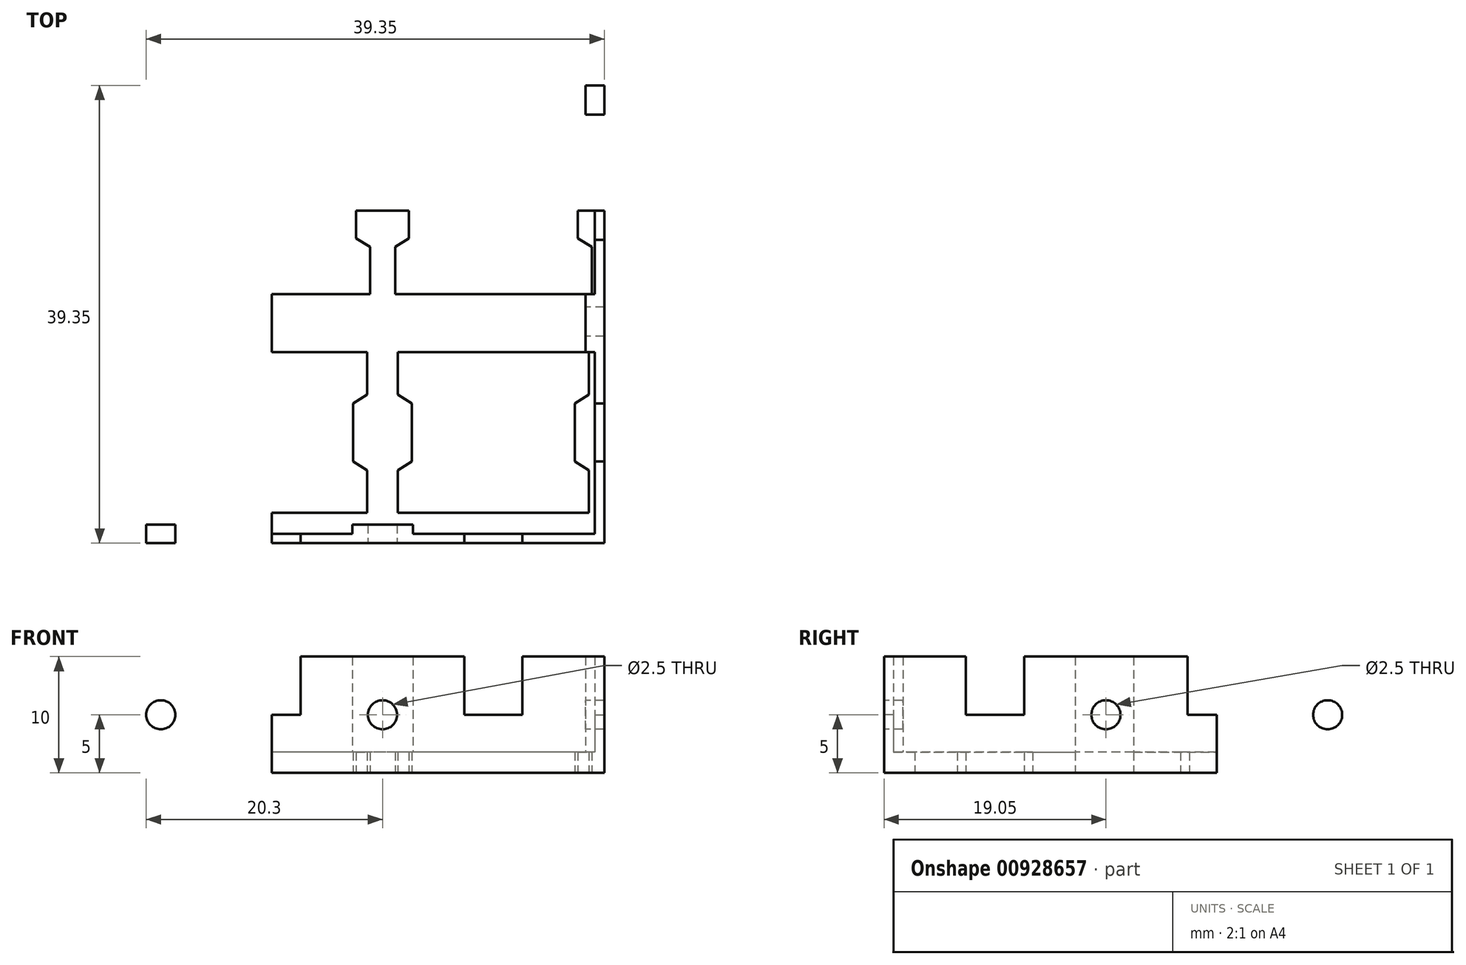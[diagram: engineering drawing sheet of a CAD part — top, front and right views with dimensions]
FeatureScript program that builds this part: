
annotation { "Feature Type Name" : "Feature", "Feature Type Description" : "" }
export const myFeature = defineFeature(function(context is Context, id is Id, definition is map)
    precondition{}
    {
        {
            var Q0;
            Q0=qCreatedBy(makeId("Top.planeOp"),FACE);
            var sketch = newSketch(context, id + "F0", { "sketchPlane" : qUnion([Q0])});
            skLineSegment(sketch, "E0.bottom", {"start": v(-1.32, 2.62) * mm, "end": v(-17.73, 2.63) * mm});
            skLineSegment(sketch, "E0.top", {"start": v(-1.32, 16.43) * mm, "end": v(-17.72, 16.43) * mm});
            skLineSegment(sketch, "E0.left", {"start": v(-1.33, 2.63) * mm, "end": v(-1.32, 16.43) * mm});
            skLineSegment(sketch, "E0.right", {"start": v(-17.73, 2.63) * mm, "end": v(-17.73, 16.43) * mm});
            skLineSegment(sketch, "E1", {"start": v(-1.32, 12.78) * mm, "end": v(-2.53, 12.02) * mm});
            skLineSegment(sketch, "E2", {"start": v(-2.53, 12.02) * mm, "end": v(-2.53, 7.03) * mm});
            skLineSegment(sketch, "E3", {"start": v(-2.53, 7.02) * mm, "end": v(-1.32, 6.27) * mm});
            skLineSegment(sketch, "E4", {"start": v(-1.32, 6.27) * mm, "end": v(-1.32, 12.78) * mm});
            skLineSegment(sketch, "E5", {"start": v(-1.32, 12.78) * mm, "end": v(-1.32, 16.43) * mm});
            skLineSegment(sketch, "E6", {"start": v(-1.32, 6.27) * mm, "end": v(-1.33, 2.62) * mm});
            skLineSegment(sketch, "E7", {"start": v(-9.52, 16.43) * mm, "end": v(-9.53, 2.63) * mm});
            skLineSegment(sketch, "E8.MirrorCS", {"start": v(-16.52, 12.03) * mm, "end": v(-16.52, 7.03) * mm});
            skLineSegment(sketch, "E9.MirrorCS", {"start": v(-17.73, 12.78) * mm, "end": v(-16.52, 12.03) * mm});
            skLineSegment(sketch, "E10.MirrorCS", {"start": v(-16.52, 7.03) * mm, "end": v(-17.73, 6.28) * mm});
            skLineSegment(sketch, "E11.1.0.0", {"start": v(-20.38, 16.43) * mm, "end": v(-36.78, 16.43) * mm});
            skLineSegment(sketch, "E11.1.0.1", {"start": v(-36.78, 2.63) * mm, "end": v(-36.78, 16.43) * mm});
            skLineSegment(sketch, "E11.1.0.2", {"start": v(-20.38, 2.63) * mm, "end": v(-36.78, 2.63) * mm});
            skLineSegment(sketch, "E11.1.0.3", {"start": v(-20.38, 6.28) * mm, "end": v(-20.38, 2.63) * mm});
            skLineSegment(sketch, "E11.1.0.4", {"start": v(-21.58, 12.03) * mm, "end": v(-21.58, 7.03) * mm});
            skLineSegment(sketch, "E11.1.0.5", {"start": v(-21.58, 7.03) * mm, "end": v(-20.38, 6.28) * mm});
            skLineSegment(sketch, "E11.1.0.6", {"start": v(-20.38, 12.78) * mm, "end": v(-21.58, 12.03) * mm});
            skLineSegment(sketch, "E11.1.0.7", {"start": v(-20.37, 12.78) * mm, "end": v(-20.37, 16.43) * mm});
            skLineSegment(sketch, "E11.1.0.8", {"start": v(-20.38, 6.28) * mm, "end": v(-20.38, 12.78) * mm});
            skLineSegment(sketch, "E11.1.0.9", {"start": v(-35.57, 12.03) * mm, "end": v(-35.57, 7.03) * mm});
            skLineSegment(sketch, "E11.1.0.10", {"start": v(-36.78, 12.78) * mm, "end": v(-35.57, 12.03) * mm});
            skLineSegment(sketch, "E11.1.0.11", {"start": v(-35.57, 7.03) * mm, "end": v(-36.78, 6.28) * mm});
            skLineSegment(sketch, "E11.2.0.0", {"start": v(-39.43, 16.43) * mm, "end": v(-55.83, 16.43) * mm});
            skLineSegment(sketch, "E11.2.0.1", {"start": v(-55.83, 2.63) * mm, "end": v(-55.83, 16.43) * mm});
            skLineSegment(sketch, "E11.2.0.2", {"start": v(-39.43, 2.63) * mm, "end": v(-55.83, 2.63) * mm});
            skLineSegment(sketch, "E11.2.0.3", {"start": v(-39.43, 6.28) * mm, "end": v(-39.43, 2.63) * mm});
            skLineSegment(sketch, "E11.2.0.4", {"start": v(-40.63, 12.03) * mm, "end": v(-40.63, 7.03) * mm});
            skLineSegment(sketch, "E11.2.0.5", {"start": v(-40.63, 7.03) * mm, "end": v(-39.43, 6.28) * mm});
            skLineSegment(sketch, "E11.2.0.6", {"start": v(-39.43, 12.78) * mm, "end": v(-40.63, 12.03) * mm});
            skLineSegment(sketch, "E11.2.0.7", {"start": v(-39.43, 12.78) * mm, "end": v(-39.43, 16.43) * mm});
            skLineSegment(sketch, "E11.2.0.8", {"start": v(-39.43, 6.28) * mm, "end": v(-39.43, 12.78) * mm});
            skLineSegment(sketch, "E11.2.0.9", {"start": v(-54.62, 12.03) * mm, "end": v(-54.62, 7.03) * mm});
            skLineSegment(sketch, "E11.2.0.10", {"start": v(-55.83, 12.78) * mm, "end": v(-54.62, 12.03) * mm});
            skLineSegment(sketch, "E11.2.0.11", {"start": v(-54.62, 7.03) * mm, "end": v(-55.83, 6.28) * mm});
            skLineSegment(sketch, "E11.direction1", {"start": v(-17.72, 16.43) * mm, "end": v(-36.78, 16.43) * mm, "construction": true});
            skLineSegment(sketch, "E12.bottom", {"start": v(0, 0) * mm, "end": v(-57.15, 0) * mm});
            skLineSegment(sketch, "E12.top", {"start": v(0, 57.15) * mm, "end": v(-57.15, 57.15) * mm});
            skLineSegment(sketch, "E12.left", {"start": v(0, 0) * mm, "end": v(0, 57.15) * mm});
            skLineSegment(sketch, "E12.right", {"start": v(-57.15, 0) * mm, "end": v(-57.15, 57.15) * mm});
            skLineSegment(sketch, "E13", {"start": v(-1.32, 2.62) * mm, "end": v(0, 2.62) * mm});
            skLineSegment(sketch, "E14", {"start": v(-55.83, 2.63) * mm, "end": v(-57.15, 2.63) * mm});
            skLineSegment(sketch, "E15", {"start": v(-1.33, 2.62) * mm, "end": v(-1.33, 0) * mm});
            skLineSegment(sketch, "E16.0.1.0", {"start": v(-39.42, 31.83) * mm, "end": v(-39.42, 35.48) * mm});
            skLineSegment(sketch, "E16.0.1.1", {"start": v(-20.37, 25.33) * mm, "end": v(-20.37, 21.68) * mm});
            skLineSegment(sketch, "E16.0.1.3", {"start": v(-40.62, 31.08) * mm, "end": v(-40.62, 26.08) * mm});
            skLineSegment(sketch, "E16.0.1.4", {"start": v(-1.32, 35.48) * mm, "end": v(-17.72, 35.48) * mm});
            skLineSegment(sketch, "E16.0.1.5", {"start": v(-1.32, 31.82) * mm, "end": v(-1.32, 35.48) * mm});
            skLineSegment(sketch, "E16.0.1.6", {"start": v(-1.32, 21.67) * mm, "end": v(-17.73, 21.68) * mm});
            skLineSegment(sketch, "E16.0.1.7", {"start": v(-39.42, 21.68) * mm, "end": v(-55.82, 21.68) * mm});
            skLineSegment(sketch, "E16.0.1.8", {"start": v(-35.57, 31.08) * mm, "end": v(-35.57, 26.08) * mm});
            skLineSegment(sketch, "E16.0.1.9", {"start": v(-39.42, 25.33) * mm, "end": v(-39.42, 21.68) * mm});
            skLineSegment(sketch, "E16.0.1.10", {"start": v(-21.57, 31.08) * mm, "end": v(-21.57, 26.08) * mm});
            skLineSegment(sketch, "E16.0.1.11", {"start": v(-20.37, 31.83) * mm, "end": v(-20.37, 35.48) * mm});
            skLineSegment(sketch, "E16.0.1.12", {"start": v(-20.37, 21.68) * mm, "end": v(-36.77, 21.68) * mm});
            skLineSegment(sketch, "E16.0.1.13", {"start": v(-54.62, 31.08) * mm, "end": v(-54.62, 26.08) * mm});
            skLineSegment(sketch, "E16.0.1.14", {"start": v(-20.37, 25.33) * mm, "end": v(-20.37, 31.83) * mm});
            skLineSegment(sketch, "E16.0.1.15", {"start": v(-2.52, 31.07) * mm, "end": v(-2.53, 26.07) * mm});
            skLineSegment(sketch, "E16.0.1.16", {"start": v(-16.52, 31.08) * mm, "end": v(-16.52, 26.08) * mm});
            skLineSegment(sketch, "E16.0.1.18", {"start": v(-1.32, 25.32) * mm, "end": v(-1.32, 21.68) * mm});
            skLineSegment(sketch, "E16.0.1.19", {"start": v(-39.42, 35.48) * mm, "end": v(-55.82, 35.48) * mm});
            skLineSegment(sketch, "E16.0.1.20", {"start": v(-1.32, 25.32) * mm, "end": v(-1.32, 31.82) * mm});
            skLineSegment(sketch, "E16.0.1.21", {"start": v(-17.72, 31.83) * mm, "end": v(-16.52, 31.08) * mm});
            skLineSegment(sketch, "E16.0.1.22", {"start": v(-36.77, 31.83) * mm, "end": v(-35.57, 31.08) * mm});
            skLineSegment(sketch, "E16.0.1.23", {"start": v(-1.32, 31.82) * mm, "end": v(-2.52, 31.07) * mm});
            skLineSegment(sketch, "E16.0.1.24", {"start": v(-20.37, 35.48) * mm, "end": v(-36.77, 35.48) * mm});
            skLineSegment(sketch, "E16.0.1.25", {"start": v(-16.52, 26.08) * mm, "end": v(-17.72, 25.33) * mm});
            skLineSegment(sketch, "E16.0.1.27", {"start": v(-2.52, 26.08) * mm, "end": v(-1.32, 25.32) * mm});
            skLineSegment(sketch, "E16.0.1.28", {"start": v(-35.57, 26.08) * mm, "end": v(-36.77, 25.33) * mm});
            skLineSegment(sketch, "E16.0.1.29", {"start": v(-40.62, 26.08) * mm, "end": v(-39.42, 25.33) * mm});
            skLineSegment(sketch, "E16.0.1.30", {"start": v(-20.37, 31.83) * mm, "end": v(-21.57, 31.08) * mm});
            skLineSegment(sketch, "E16.0.1.31", {"start": v(-55.83, 31.83) * mm, "end": v(-54.62, 31.08) * mm});
            skLineSegment(sketch, "E16.0.1.32", {"start": v(-21.57, 26.08) * mm, "end": v(-20.37, 25.33) * mm});
            skLineSegment(sketch, "E16.0.1.33", {"start": v(-39.42, 31.83) * mm, "end": v(-40.62, 31.08) * mm});
            skLineSegment(sketch, "E16.0.1.34", {"start": v(-54.62, 26.08) * mm, "end": v(-55.82, 25.33) * mm});
            skLineSegment(sketch, "E16.0.1.36", {"start": v(-39.42, 25.33) * mm, "end": v(-39.42, 31.83) * mm});
            skLineSegment(sketch, "E16.0.2.0", {"start": v(-39.42, 50.88) * mm, "end": v(-39.42, 54.53) * mm});
            skLineSegment(sketch, "E16.0.2.1", {"start": v(-20.37, 44.38) * mm, "end": v(-20.37, 40.73) * mm});
            skLineSegment(sketch, "E16.0.2.2", {"start": v(-17.72, 40.73) * mm, "end": v(-17.72, 54.53) * mm});
            skLineSegment(sketch, "E16.0.2.3", {"start": v(-40.62, 50.13) * mm, "end": v(-40.62, 45.13) * mm});
            skLineSegment(sketch, "E16.0.2.4", {"start": v(-1.32, 54.52) * mm, "end": v(-17.72, 54.52) * mm});
            skLineSegment(sketch, "E16.0.2.5", {"start": v(-1.32, 50.88) * mm, "end": v(-1.32, 54.53) * mm});
            skLineSegment(sketch, "E16.0.2.6", {"start": v(-1.32, 40.72) * mm, "end": v(-17.72, 40.72) * mm});
            skLineSegment(sketch, "E16.0.2.7", {"start": v(-39.42, 40.73) * mm, "end": v(-55.82, 40.73) * mm});
            skLineSegment(sketch, "E16.0.2.8", {"start": v(-35.57, 50.12) * mm, "end": v(-35.57, 45.13) * mm});
            skLineSegment(sketch, "E16.0.2.9", {"start": v(-39.42, 44.38) * mm, "end": v(-39.42, 40.73) * mm});
            skLineSegment(sketch, "E16.0.2.10", {"start": v(-21.57, 50.12) * mm, "end": v(-21.57, 45.13) * mm});
            skLineSegment(sketch, "E16.0.2.11", {"start": v(-20.37, 50.88) * mm, "end": v(-20.37, 54.53) * mm});
            skLineSegment(sketch, "E16.0.2.12", {"start": v(-20.37, 40.72) * mm, "end": v(-36.77, 40.72) * mm});
            skLineSegment(sketch, "E16.0.2.13", {"start": v(-54.62, 50.13) * mm, "end": v(-54.62, 45.13) * mm});
            skLineSegment(sketch, "E16.0.2.14", {"start": v(-20.37, 44.38) * mm, "end": v(-20.37, 50.88) * mm});
            skLineSegment(sketch, "E16.0.2.15", {"start": v(-2.52, 50.12) * mm, "end": v(-2.52, 45.12) * mm});
            skLineSegment(sketch, "E16.0.2.16", {"start": v(-16.52, 50.12) * mm, "end": v(-16.52, 45.13) * mm});
            skLineSegment(sketch, "E16.0.2.17", {"start": v(-36.77, 40.73) * mm, "end": v(-36.77, 54.53) * mm});
            skLineSegment(sketch, "E16.0.2.18", {"start": v(-1.32, 44.38) * mm, "end": v(-1.32, 40.73) * mm});
            skLineSegment(sketch, "E16.0.2.19", {"start": v(-39.42, 54.53) * mm, "end": v(-55.82, 54.53) * mm});
            skLineSegment(sketch, "E16.0.2.20", {"start": v(-1.32, 44.38) * mm, "end": v(-1.32, 50.88) * mm});
            skLineSegment(sketch, "E16.0.2.21", {"start": v(-17.72, 50.88) * mm, "end": v(-16.52, 50.13) * mm});
            skLineSegment(sketch, "E16.0.2.22", {"start": v(-36.77, 50.88) * mm, "end": v(-35.57, 50.12) * mm});
            skLineSegment(sketch, "E16.0.2.23", {"start": v(-1.32, 50.88) * mm, "end": v(-2.52, 50.12) * mm});
            skLineSegment(sketch, "E16.0.2.24", {"start": v(-20.37, 54.52) * mm, "end": v(-36.77, 54.52) * mm});
            skLineSegment(sketch, "E16.0.2.25", {"start": v(-16.52, 45.13) * mm, "end": v(-17.72, 44.38) * mm});
            skLineSegment(sketch, "E16.0.2.26", {"start": v(-1.32, 40.73) * mm, "end": v(-1.32, 54.53) * mm});
            skLineSegment(sketch, "E16.0.2.27", {"start": v(-2.52, 45.12) * mm, "end": v(-1.32, 44.38) * mm});
            skLineSegment(sketch, "E16.0.2.28", {"start": v(-35.57, 45.13) * mm, "end": v(-36.77, 44.38) * mm});
            skLineSegment(sketch, "E16.0.2.29", {"start": v(-40.62, 45.13) * mm, "end": v(-39.42, 44.38) * mm});
            skLineSegment(sketch, "E16.0.2.30", {"start": v(-20.37, 50.88) * mm, "end": v(-21.57, 50.13) * mm});
            skLineSegment(sketch, "E16.0.2.31", {"start": v(-55.83, 50.88) * mm, "end": v(-54.62, 50.13) * mm});
            skLineSegment(sketch, "E16.0.2.32", {"start": v(-21.57, 45.12) * mm, "end": v(-20.37, 44.38) * mm});
            skLineSegment(sketch, "E16.0.2.33", {"start": v(-39.42, 50.88) * mm, "end": v(-40.62, 50.12) * mm});
            skLineSegment(sketch, "E16.0.2.34", {"start": v(-54.62, 45.13) * mm, "end": v(-55.82, 44.38) * mm});
            skLineSegment(sketch, "E16.0.2.35", {"start": v(-55.82, 40.73) * mm, "end": v(-55.82, 54.53) * mm});
            skLineSegment(sketch, "E16.0.2.36", {"start": v(-39.42, 44.38) * mm, "end": v(-39.42, 50.88) * mm});
            skLineSegment(sketch, "E16.direction1", {"start": v(-55.83, 2.63) * mm, "end": v(-33.77, 2.63) * mm, "construction": true});
            skLineSegment(sketch, "E16.direction2", {"start": v(-55.83, 2.63) * mm, "end": v(-55.83, 21.68) * mm, "construction": true});
            skLineSegment(sketch, "E17", {"start": v(-1.32, 54.53) * mm, "end": v(-1.32, 57.15) * mm});
            skLineSegment(sketch, "E18", {"start": v(-55.83, 12.78) * mm, "end": v(-55.83, 16.43) * mm});
            skLineSegment(sketch, "E19", {"start": v(-55.83, 31.83) * mm, "end": v(-55.83, 35.48) * mm});
            skLineSegment(sketch, "E20", {"start": v(-55.83, 25.33) * mm, "end": v(-55.83, 21.68) * mm});
            skLineSegment(sketch, "E21", {"start": v(-36.77, 25.33) * mm, "end": v(-36.77, 21.68) * mm});
            skLineSegment(sketch, "E22", {"start": v(-36.77, 31.83) * mm, "end": v(-36.77, 35.48) * mm});
            skLineSegment(sketch, "E23", {"start": v(-17.72, 35.48) * mm, "end": v(-17.72, 31.83) * mm});
            skLineSegment(sketch, "E24", {"start": v(-17.72, 25.33) * mm, "end": v(-17.72, 21.68) * mm});
            skLineSegment(sketch, "E25", {"start": v(-55.83, 31.83) * mm, "end": v(-55.83, 25.33) * mm});
            skLineSegment(sketch, "E26", {"start": v(-36.77, 25.33) * mm, "end": v(-36.77, 31.83) * mm});
            skLineSegment(sketch, "E27", {"start": v(-17.72, 25.33) * mm, "end": v(-17.72, 31.83) * mm});
            skLineSegment(sketch, "E28.0", {"start": v(-39.17, 31.69) * mm, "end": v(-39.17, 35.73) * mm});
            skLineSegment(sketch, "E28.1", {"start": v(-54.87, 26.21) * mm, "end": v(-56.08, 25.46) * mm});
            skLineSegment(sketch, "E28.2", {"start": v(-54.87, 30.94) * mm, "end": v(-54.87, 26.21) * mm});
            skLineSegment(sketch, "E28.3", {"start": v(-56.08, 31.69) * mm, "end": v(-54.87, 30.94) * mm});
            skLineSegment(sketch, "E28.4", {"start": v(-56.08, 31.69) * mm, "end": v(-56.08, 35.73) * mm});
            skLineSegment(sketch, "E28.5", {"start": v(-56.08, 25.46) * mm, "end": v(-56.08, 21.43) * mm});
            skLineSegment(sketch, "E28.6", {"start": v(-39.17, 35.73) * mm, "end": v(-56.08, 35.73) * mm});
            skLineSegment(sketch, "E28.7", {"start": v(-39.17, 21.43) * mm, "end": v(-56.08, 21.43) * mm});
            skLineSegment(sketch, "E28.8", {"start": v(-39.17, 25.46) * mm, "end": v(-39.17, 21.43) * mm});
            skLineSegment(sketch, "E28.9", {"start": v(-40.38, 26.21) * mm, "end": v(-39.17, 25.46) * mm});
            skLineSegment(sketch, "E28.10", {"start": v(-40.38, 30.94) * mm, "end": v(-40.38, 26.21) * mm});
            skLineSegment(sketch, "E28.11", {"start": v(-39.17, 31.69) * mm, "end": v(-40.38, 30.94) * mm});
            skLineSegment(sketch, "E29.0", {"start": v(-20.12, 31.69) * mm, "end": v(-20.12, 35.73) * mm});
            skLineSegment(sketch, "E29.1", {"start": v(-35.82, 26.21) * mm, "end": v(-37.02, 25.46) * mm});
            skLineSegment(sketch, "E29.2", {"start": v(-35.82, 30.94) * mm, "end": v(-35.82, 26.21) * mm});
            skLineSegment(sketch, "E29.3", {"start": v(-37.02, 31.69) * mm, "end": v(-35.82, 30.94) * mm});
            skLineSegment(sketch, "E29.4", {"start": v(-37.02, 31.69) * mm, "end": v(-37.02, 35.73) * mm});
            skLineSegment(sketch, "E29.5", {"start": v(-37.02, 25.46) * mm, "end": v(-37.02, 21.43) * mm});
            skLineSegment(sketch, "E29.6", {"start": v(-20.12, 35.73) * mm, "end": v(-37.02, 35.73) * mm});
            skLineSegment(sketch, "E29.7", {"start": v(-20.12, 21.43) * mm, "end": v(-37.02, 21.43) * mm});
            skLineSegment(sketch, "E29.8", {"start": v(-20.12, 25.46) * mm, "end": v(-20.12, 21.43) * mm});
            skLineSegment(sketch, "E29.9", {"start": v(-21.32, 26.21) * mm, "end": v(-20.12, 25.46) * mm});
            skLineSegment(sketch, "E29.10", {"start": v(-21.32, 30.94) * mm, "end": v(-21.32, 26.21) * mm});
            skLineSegment(sketch, "E29.11", {"start": v(-20.12, 31.69) * mm, "end": v(-21.32, 30.94) * mm});
            skLineSegment(sketch, "E30.0", {"start": v(-1.07, 31.69) * mm, "end": v(-1.07, 35.73) * mm});
            skLineSegment(sketch, "E30.1", {"start": v(-16.77, 26.21) * mm, "end": v(-17.97, 25.46) * mm});
            skLineSegment(sketch, "E30.2", {"start": v(-16.77, 30.94) * mm, "end": v(-16.77, 26.21) * mm});
            skLineSegment(sketch, "E30.3", {"start": v(-17.97, 31.69) * mm, "end": v(-16.77, 30.94) * mm});
            skLineSegment(sketch, "E30.4", {"start": v(-17.97, 35.73) * mm, "end": v(-17.97, 31.69) * mm});
            skLineSegment(sketch, "E30.5", {"start": v(-17.97, 25.46) * mm, "end": v(-17.97, 21.43) * mm});
            skLineSegment(sketch, "E30.6", {"start": v(-1.07, 35.73) * mm, "end": v(-17.97, 35.73) * mm});
            skLineSegment(sketch, "E30.7", {"start": v(-1.07, 21.43) * mm, "end": v(-17.97, 21.43) * mm});
            skLineSegment(sketch, "E30.8", {"start": v(-1.07, 25.46) * mm, "end": v(-1.08, 21.43) * mm});
            skLineSegment(sketch, "E30.9", {"start": v(-2.28, 26.21) * mm, "end": v(-1.08, 25.46) * mm});
            skLineSegment(sketch, "E30.10", {"start": v(-2.27, 30.94) * mm, "end": v(-2.28, 26.21) * mm});
            skLineSegment(sketch, "E30.11", {"start": v(-1.08, 31.69) * mm, "end": v(-2.28, 30.94) * mm});
            skSolve(sketch);
        }
        {
            var Q0;
            {var subQ4=sQuery(id+"F0.wireOp",EDGE,"E13");Q0=makeQuery(id+"F0.imprint","IMPRINT",FACE,{"disambiguationData":[TD([[makeQuery(id+"F0.imprint","IMPRINT",EDGE,{"derivedFrom":subQ4}),-1.0]])]});}
            var Q1;
            Q1=makeQuery(id+"F0.imprint","IMPRINT",FACE,{"disambiguationData":[TD([[makeQuery(id+"F0.imprint","IMPRINT",EDGE,{"derivedFrom":sQuery(id+"F0.wireOp",EDGE,"E11.1.0.9")}),-1.0]])]});
            var Q2;
            Q2=makeQuery(id+"F0.imprint","IMPRINT",FACE,{"disambiguationData":[TD([[makeQuery(id+"F0.imprint","IMPRINT",EDGE,{"derivedFrom":sQuery(id+"F0.wireOp",EDGE,"E11.2.0.4")}),1.0]])]});
            var Q3;
            Q3=makeQuery(id+"F0.imprint","IMPRINT",FACE,{"disambiguationData":[TD([[makeQuery(id+"F0.imprint","IMPRINT",EDGE,{"derivedFrom":sQuery(id+"F0.wireOp",EDGE,"437544f1-30d8-4290-8c43-db503dbb5188.0.1.24")}),-1.0]])]});
            var Q4;
            Q4=makeQuery(id+"F0.imprint","IMPRINT",FACE,{"disambiguationData":[TD([[makeQuery(id+"F0.imprint","IMPRINT",EDGE,{"derivedFrom":sQuery(id+"F0.wireOp",EDGE,"437544f1-30d8-4290-8c43-db503dbb5188.0.1.14")}),1.0]])]});
            var Q5;
            Q5=makeQuery(id+"F0.imprint","IMPRINT",FACE,{"disambiguationData":[TD([[makeQuery(id+"F0.imprint","IMPRINT",EDGE,{"derivedFrom":sQuery(id+"F0.wireOp",EDGE,"437544f1-30d8-4290-8c43-db503dbb5188.0.1.10")}),-1.0]])]});
            var Q6;
            Q6=makeQuery(id+"F0.imprint","IMPRINT",FACE,{"disambiguationData":[TD([[makeQuery(id+"F0.imprint","IMPRINT",EDGE,{"derivedFrom":sQuery(id+"F0.wireOp",EDGE,"437544f1-30d8-4290-8c43-db503dbb5188.0.1.7")}),1.0]])]});
            var Q7;
            Q7=makeQuery(id+"F0.imprint","IMPRINT",FACE,{"disambiguationData":[TD([[makeQuery(id+"F0.imprint","IMPRINT",EDGE,{"derivedFrom":sQuery(id+"F0.wireOp",EDGE,"437544f1-30d8-4290-8c43-db503dbb5188.0.1.3")}),-1.0]])]});
            var Q8;
            Q8=makeQuery(id+"F0.imprint","IMPRINT",FACE,{"disambiguationData":[TD([[makeQuery(id+"F0.imprint","IMPRINT",EDGE,{"derivedFrom":sQuery(id+"F0.wireOp",EDGE,"437544f1-30d8-4290-8c43-db503dbb5188.0.1.4")}),1.0]])]});
            var Q9;
            Q9=makeQuery(id+"F0.imprint","IMPRINT",FACE,{"disambiguationData":[TD([[makeQuery(id+"F0.imprint","IMPRINT",EDGE,{"derivedFrom":sQuery(id+"F0.wireOp",EDGE,"437544f1-30d8-4290-8c43-db503dbb5188.0.2.4")}),1.0]])]});
            var Q10;
            Q10=makeQuery(id+"F0.imprint","IMPRINT",FACE,{"disambiguationData":[TD([[makeQuery(id+"F0.imprint","IMPRINT",EDGE,{"derivedFrom":sQuery(id+"F0.wireOp",EDGE,"437544f1-30d8-4290-8c43-db503dbb5188.0.2.3")}),-1.0]])]});
            var Q11;
            Q11=makeQuery(id+"F0.imprint","IMPRINT",FACE,{"disambiguationData":[TD([[makeQuery(id+"F0.imprint","IMPRINT",EDGE,{"derivedFrom":sQuery(id+"F0.wireOp",EDGE,"437544f1-30d8-4290-8c43-db503dbb5188.0.2.7")}),1.0]])]});
            var Q12;
            Q12=makeQuery(id+"F0.imprint","IMPRINT",FACE,{"disambiguationData":[TD([[makeQuery(id+"F0.imprint","IMPRINT",EDGE,{"derivedFrom":sQuery(id+"F0.wireOp",EDGE,"437544f1-30d8-4290-8c43-db503dbb5188.0.2.10")}),-1.0]])]});
            var Q13;
            Q13=makeQuery(id+"F0.imprint","IMPRINT",FACE,{"disambiguationData":[TD([[makeQuery(id+"F0.imprint","IMPRINT",EDGE,{"derivedFrom":sQuery(id+"F0.wireOp",EDGE,"437544f1-30d8-4290-8c43-db503dbb5188.0.2.14")}),1.0]])]});
            var Q14;
            Q14=makeQuery(id+"F0.imprint","IMPRINT",FACE,{"disambiguationData":[TD([[makeQuery(id+"F0.imprint","IMPRINT",EDGE,{"derivedFrom":sQuery(id+"F0.wireOp",EDGE,"437544f1-30d8-4290-8c43-db503dbb5188.0.2.24")}),-1.0]])]});
            var Q15;
            {var subQ71=sQuery(id+"F0.wireOp",EDGE,"E11.1.0.0");Q15=makeQuery(id+"F0.imprint","IMPRINT",FACE,{"disambiguationData":[TD([[makeQuery(id+"F0.imprint","IMPRINT",EDGE,{"derivedFrom":subQ71}),-1.0]])]});}
            var Q16;
            Q16=makeQuery(id+"F0.imprint","IMPRINT",FACE,{"disambiguationData":[TD([[makeQuery(id+"F0.imprint","IMPRINT",EDGE,{"derivedFrom":sQuery(id+"F0.wireOp",EDGE,"E8.MirrorCS")}),-1.0]])]});
            var Q17;
            Q17=makeQuery(id+"F0.imprint","IMPRINT",FACE,{"disambiguationData":[TD([[makeQuery(id+"F0.imprint","IMPRINT",EDGE,{"derivedFrom":sQuery(id+"F0.wireOp",EDGE,"E11.1.0.4")}),1.0]])]});
            var Q18;
            Q18=makeQuery(id+"F0.imprint","IMPRINT",FACE,{"disambiguationData":[TD([[makeQuery(id+"F0.imprint","IMPRINT",EDGE,{"derivedFrom":sQuery(id+"F0.wireOp",EDGE,"E16.0.2.8")}),-1.0]])]});
            var Q19;
            Q19=makeQuery(id+"F0.imprint","IMPRINT",FACE,{"disambiguationData":[TD([[makeQuery(id+"F0.imprint","IMPRINT",EDGE,{"derivedFrom":sQuery(id+"F0.wireOp",EDGE,"E16.0.2.15")}),1.0]])]});
            var Q20;
            {var subQ2=sQuery(id+"F0.wireOp",EDGE,"E1");Q20=makeQuery(id+"F0.imprint","IMPRINT",FACE,{"disambiguationData":[TD([[makeQuery(id+"F0.imprint","IMPRINT",EDGE,{"derivedFrom":subQ2}),1.0]])]});}
            var Q21;
            Q21=makeQuery(id+"F0.imprint","IMPRINT",FACE,{"disambiguationData":[TD([[makeQuery(id+"F0.imprint","IMPRINT",EDGE,{"derivedFrom":sQuery(id+"F0.wireOp",EDGE,"E11.2.0.9")}),-1.0]])]});
            var Q22;
            Q22=makeQuery(id+"F0.imprint","IMPRINT",FACE,{"disambiguationData":[TD([[makeQuery(id+"F0.imprint","IMPRINT",EDGE,{"derivedFrom":sQuery(id+"F0.wireOp",EDGE,"E16.0.2.16")}),-1.0]])]});
            var Q23;
            Q23=makeQuery(id+"F0.imprint","IMPRINT",FACE,{"disambiguationData":[TD([[makeQuery(id+"F0.imprint","IMPRINT",EDGE,{"derivedFrom":sQuery(id+"F0.wireOp",EDGE,"E16.0.2.10")}),1.0]])]});
            var Q24;
            Q24=makeQuery(id+"F0.imprint","IMPRINT",FACE,{"disambiguationData":[TD([[makeQuery(id+"F0.imprint","IMPRINT",EDGE,{"derivedFrom":sQuery(id+"F0.wireOp",EDGE,"E16.0.2.3")}),1.0]])]});
            var Q25;
            Q25=makeQuery(id+"F0.imprint","IMPRINT",FACE,{"disambiguationData":[TD([[makeQuery(id+"F0.imprint","IMPRINT",EDGE,{"derivedFrom":sQuery(id+"F0.wireOp",EDGE,"E16.0.2.13")}),-1.0]])]});
            var Q26;
            {var subQ5=sQuery(id+"F0.wireOp",EDGE,"E28.2");Q26=makeQuery(id+"F0.imprint","IMPRINT",FACE,{"disambiguationData":[TD([[makeQuery(id+"F0.imprint","IMPRINT",EDGE,{"derivedFrom":subQ5}),-1.0]])]});}
            var Q27;
            {var subQ5=sQuery(id+"F0.wireOp",EDGE,"E28.10");Q27=makeQuery(id+"F0.imprint","IMPRINT",FACE,{"disambiguationData":[TD([[makeQuery(id+"F0.imprint","IMPRINT",EDGE,{"derivedFrom":subQ5}),1.0]])]});}
            var Q28;
            {var subQ5=sQuery(id+"F0.wireOp",EDGE,"E29.2");Q28=makeQuery(id+"F0.imprint","IMPRINT",FACE,{"disambiguationData":[TD([[makeQuery(id+"F0.imprint","IMPRINT",EDGE,{"derivedFrom":subQ5}),-1.0]])]});}
            var Q29;
            {var subQ5=sQuery(id+"F0.wireOp",EDGE,"E29.10");Q29=makeQuery(id+"F0.imprint","IMPRINT",FACE,{"disambiguationData":[TD([[makeQuery(id+"F0.imprint","IMPRINT",EDGE,{"derivedFrom":subQ5}),1.0]])]});}
            var Q30;
            {var subQ5=sQuery(id+"F0.wireOp",EDGE,"E30.2");Q30=makeQuery(id+"F0.imprint","IMPRINT",FACE,{"disambiguationData":[TD([[makeQuery(id+"F0.imprint","IMPRINT",EDGE,{"derivedFrom":subQ5}),-1.0]])]});}
            var Q31;
            {var subQ5=sQuery(id+"F0.wireOp",EDGE,"E30.10");Q31=makeQuery(id+"F0.imprint","IMPRINT",FACE,{"disambiguationData":[TD([[makeQuery(id+"F0.imprint","IMPRINT",EDGE,{"derivedFrom":subQ5}),1.0]])]});}
            extrude(context, id + "F1", {"entities" : qUnion([Q0, Q1, Q2, Q3, Q4, Q5, Q6, Q7, Q8, Q9, Q10, Q11, Q12, Q13, Q14, Q15, Q16, Q17, Q18, Q19, Q20, Q21, Q22, Q23, Q24, Q25, Q26, Q27, Q28, Q29, Q30, Q31]), "depth" : 1.8 * mm, "offsetDistance" : 25 * mm});
        }
        {
            var Q0;
            Q0=makeQuery(id+"F1.opExtrude","CAP_FACE",FACE,{"disambiguationData":[OSD([sQuery(id+"F0.wireOp",EDGE,"E0.bottom"),sQuery(id+"F0.wireOp",EDGE,"E0.top"),sQuery(id+"F0.wireOp",EDGE,"E0.left"),sQuery(id+"F0.wireOp",EDGE,"E0.right"),sQuery(id+"F0.wireOp",EDGE,"E1"),sQuery(id+"F0.wireOp",EDGE,"E2"),sQuery(id+"F0.wireOp",EDGE,"E3"),sQuery(id+"F0.wireOp",EDGE,"E8.MirrorCS"),sQuery(id+"F0.wireOp",EDGE,"E9.MirrorCS"),sQuery(id+"F0.wireOp",EDGE,"E10.MirrorCS"),sQuery(id+"F0.wireOp",EDGE,"E11.1.0.0"),sQuery(id+"F0.wireOp",EDGE,"E11.1.0.1"),sQuery(id+"F0.wireOp",EDGE,"E11.1.0.2"),sQuery(id+"F0.wireOp",EDGE,"E11.1.0.3"),sQuery(id+"F0.wireOp",EDGE,"E11.1.0.4"),sQuery(id+"F0.wireOp",EDGE,"E11.1.0.5"),sQuery(id+"F0.wireOp",EDGE,"E11.1.0.6"),sQuery(id+"F0.wireOp",EDGE,"E11.1.0.7"),sQuery(id+"F0.wireOp",EDGE,"E11.1.0.9"),sQuery(id+"F0.wireOp",EDGE,"E11.1.0.10"),sQuery(id+"F0.wireOp",EDGE,"E11.1.0.11"),sQuery(id+"F0.wireOp",EDGE,"E11.2.0.0"),sQuery(id+"F0.wireOp",EDGE,"E11.2.0.1"),sQuery(id+"F0.wireOp",EDGE,"E11.2.0.2"),sQuery(id+"F0.wireOp",EDGE,"E11.2.0.3"),sQuery(id+"F0.wireOp",EDGE,"E11.2.0.4"),sQuery(id+"F0.wireOp",EDGE,"E11.2.0.5"),sQuery(id+"F0.wireOp",EDGE,"E11.2.0.6"),sQuery(id+"F0.wireOp",EDGE,"E11.2.0.7"),sQuery(id+"F0.wireOp",EDGE,"E11.2.0.9"),sQuery(id+"F0.wireOp",EDGE,"E11.2.0.10"),sQuery(id+"F0.wireOp",EDGE,"E11.2.0.11"),sQuery(id+"F0.wireOp",EDGE,"E12.bottom"),sQuery(id+"F0.wireOp",EDGE,"E12.top"),sQuery(id+"F0.wireOp",EDGE,"E12.left"),sQuery(id+"F0.wireOp",EDGE,"E12.right"),sQuery(id+"F0.wireOp",EDGE,"E16.0.2.0"),sQuery(id+"F0.wireOp",EDGE,"E16.0.2.1"),sQuery(id+"F0.wireOp",EDGE,"E16.0.2.2"),sQuery(id+"F0.wireOp",EDGE,"E16.0.2.3"),sQuery(id+"F0.wireOp",EDGE,"E16.0.2.4"),sQuery(id+"F0.wireOp",EDGE,"E16.0.2.5"),sQuery(id+"F0.wireOp",EDGE,"E16.0.2.6"),sQuery(id+"F0.wireOp",EDGE,"E16.0.2.7"),sQuery(id+"F0.wireOp",EDGE,"E16.0.2.8"),sQuery(id+"F0.wireOp",EDGE,"E16.0.2.9"),sQuery(id+"F0.wireOp",EDGE,"E16.0.2.10"),sQuery(id+"F0.wireOp",EDGE,"E16.0.2.11"),sQuery(id+"F0.wireOp",EDGE,"E16.0.2.12"),sQuery(id+"F0.wireOp",EDGE,"E16.0.2.13"),sQuery(id+"F0.wireOp",EDGE,"E16.0.2.15"),sQuery(id+"F0.wireOp",EDGE,"E16.0.2.16"),sQuery(id+"F0.wireOp",EDGE,"E16.0.2.17"),sQuery(id+"F0.wireOp",EDGE,"E16.0.2.18"),sQuery(id+"F0.wireOp",EDGE,"E16.0.2.19"),sQuery(id+"F0.wireOp",EDGE,"E16.0.2.21"),sQuery(id+"F0.wireOp",EDGE,"E16.0.2.22"),sQuery(id+"F0.wireOp",EDGE,"E16.0.2.23"),sQuery(id+"F0.wireOp",EDGE,"E16.0.2.24"),sQuery(id+"F0.wireOp",EDGE,"E16.0.2.25"),sQuery(id+"F0.wireOp",EDGE,"E16.0.2.27"),sQuery(id+"F0.wireOp",EDGE,"E16.0.2.28"),sQuery(id+"F0.wireOp",EDGE,"E16.0.2.29"),sQuery(id+"F0.wireOp",EDGE,"E16.0.2.30"),sQuery(id+"F0.wireOp",EDGE,"E16.0.2.31"),sQuery(id+"F0.wireOp",EDGE,"E16.0.2.32"),sQuery(id+"F0.wireOp",EDGE,"E16.0.2.33"),sQuery(id+"F0.wireOp",EDGE,"E16.0.2.34"),sQuery(id+"F0.wireOp",EDGE,"E16.0.2.35"),sQuery(id+"F0.wireOp",EDGE,"E28.0"),sQuery(id+"F0.wireOp",EDGE,"E28.1"),sQuery(id+"F0.wireOp",EDGE,"E28.2"),sQuery(id+"F0.wireOp",EDGE,"E28.3"),sQuery(id+"F0.wireOp",EDGE,"E28.4"),sQuery(id+"F0.wireOp",EDGE,"E28.5"),sQuery(id+"F0.wireOp",EDGE,"E28.6"),sQuery(id+"F0.wireOp",EDGE,"E28.7"),sQuery(id+"F0.wireOp",EDGE,"E28.8"),sQuery(id+"F0.wireOp",EDGE,"E28.9"),sQuery(id+"F0.wireOp",EDGE,"E28.10"),sQuery(id+"F0.wireOp",EDGE,"E28.11"),sQuery(id+"F0.wireOp",EDGE,"E29.0"),sQuery(id+"F0.wireOp",EDGE,"E29.1"),sQuery(id+"F0.wireOp",EDGE,"E29.2"),sQuery(id+"F0.wireOp",EDGE,"E29.3"),sQuery(id+"F0.wireOp",EDGE,"E29.4"),sQuery(id+"F0.wireOp",EDGE,"E29.5"),sQuery(id+"F0.wireOp",EDGE,"E29.6"),sQuery(id+"F0.wireOp",EDGE,"E29.7"),sQuery(id+"F0.wireOp",EDGE,"E29.8"),sQuery(id+"F0.wireOp",EDGE,"E29.9"),sQuery(id+"F0.wireOp",EDGE,"E29.10"),sQuery(id+"F0.wireOp",EDGE,"E29.11"),sQuery(id+"F0.wireOp",EDGE,"E30.0"),sQuery(id+"F0.wireOp",EDGE,"E30.1"),sQuery(id+"F0.wireOp",EDGE,"E30.2"),sQuery(id+"F0.wireOp",EDGE,"E30.3"),sQuery(id+"F0.wireOp",EDGE,"E30.4"),sQuery(id+"F0.wireOp",EDGE,"E30.5"),sQuery(id+"F0.wireOp",EDGE,"E30.6"),sQuery(id+"F0.wireOp",EDGE,"E30.7"),sQuery(id+"F0.wireOp",EDGE,"E30.8"),sQuery(id+"F0.wireOp",EDGE,"E30.9"),sQuery(id+"F0.wireOp",EDGE,"E30.10"),sQuery(id+"F0.wireOp",EDGE,"E30.11")])],"isStart":false});
            var sketch = newSketch(context, id + "F2", { "sketchPlane" : qUnion([Q0])});
            skLineSegment(sketch, "E31.bottom", {"start": v(0, 0) * mm, "end": v(-57.15, 0) * mm});
            skLineSegment(sketch, "E31.top", {"start": v(0, 57.15) * mm, "end": v(-57.15, 57.15) * mm});
            skLineSegment(sketch, "E31.left", {"start": v(0, 0) * mm, "end": v(0, 57.15) * mm});
            skLineSegment(sketch, "E31.right", {"start": v(-57.15, 0) * mm, "end": v(-57.15, 57.15) * mm});
            skLineSegment(sketch, "E32.0", {"start": v(-0.8, 56.35) * mm, "end": v(-56.35, 56.35) * mm});
            skLineSegment(sketch, "E32.1", {"start": v(-0.8, 0.8) * mm, "end": v(-0.8, 56.35) * mm});
            skLineSegment(sketch, "E32.2", {"start": v(-0.8, 0.8) * mm, "end": v(-56.35, 0.8) * mm});
            skLineSegment(sketch, "E32.3", {"start": v(-56.35, 0.8) * mm, "end": v(-56.35, 56.35) * mm});
            skLineSegment(sketch, "E33", {"start": v(-2.53, 9.52) * mm, "end": v(-0.8, 9.52) * mm});
            skLineSegment(sketch, "E34", {"start": v(-0.8, 9.52) * mm, "end": v(0, 9.52) * mm});
            skLineSegment(sketch, "E35", {"start": v(-0.8, 9.52) * mm, "end": v(-0.8, 7.02) * mm});
            skLineSegment(sketch, "E36", {"start": v(-0.8, 7.02) * mm, "end": v(0, 7.02) * mm});
            skLineSegment(sketch, "E37", {"start": v(0, 7.02) * mm, "end": v(0, 9.52) * mm});
            skLineSegment(sketch, "E38.MirrorCS", {"start": v(-0.8, 12.02) * mm, "end": v(0, 12.02) * mm});
            skLineSegment(sketch, "E39.direction2", {"start": v(-0.8, 12.02) * mm, "end": v(-0.8, 31.07) * mm, "construction": true});
            skLineSegment(sketch, "E40", {"start": v(-28.58, 0) * mm, "end": v(-28.58, 0.8) * mm});
            skLineSegment(sketch, "E41.0.1.0", {"start": v(-0.8, 31.07) * mm, "end": v(0, 31.07) * mm});
            skLineSegment(sketch, "E41.0.1.1", {"start": v(-0.8, 26.07) * mm, "end": v(0, 26.07) * mm});
            skLineSegment(sketch, "E41.0.2.0", {"start": v(-0.8, 50.12) * mm, "end": v(0, 50.12) * mm});
            skLineSegment(sketch, "E41.0.2.1", {"start": v(-0.8, 45.12) * mm, "end": v(0, 45.12) * mm});
            skLineSegment(sketch, "E41.direction1", {"start": v(-0.8, 12.02) * mm, "end": v(-9.9, 12.02) * mm, "construction": true});
            skLineSegment(sketch, "E42.MirrorCS", {"start": v(-56.35, 7.02) * mm, "end": v(-57.15, 7.02) * mm});
            skLineSegment(sketch, "E43.MirrorCS", {"start": v(-56.35, 12.03) * mm, "end": v(-57.15, 12.03) * mm});
            skLineSegment(sketch, "E44.MirrorCS", {"start": v(-56.35, 26.07) * mm, "end": v(-57.15, 26.07) * mm});
            skLineSegment(sketch, "E45.MirrorCS", {"start": v(-56.35, 31.08) * mm, "end": v(-57.15, 31.08) * mm});
            skLineSegment(sketch, "E46.MirrorCS", {"start": v(-56.35, 45.12) * mm, "end": v(-57.15, 45.12) * mm});
            skLineSegment(sketch, "E47.MirrorCS", {"start": v(-56.35, 50.12) * mm, "end": v(-57.15, 50.12) * mm});
            skLineSegment(sketch, "E48", {"start": v(-9.53, 2.63) * mm, "end": v(-9.53, 0.8) * mm});
            skLineSegment(sketch, "E49", {"start": v(-9.53, 0.8) * mm, "end": v(-9.53, 0) * mm});
            skLineSegment(sketch, "E50", {"start": v(-9.53, 0) * mm, "end": v(-7.03, 0) * mm});
            skLineSegment(sketch, "E51", {"start": v(-7.03, 0) * mm, "end": v(-7.03, 0.8) * mm});
            skLineSegment(sketch, "E52", {"start": v(-7.03, 0.8) * mm, "end": v(-9.53, 0.8) * mm});
            skLineSegment(sketch, "E53", {"start": v(-9.53, 0.8) * mm, "end": v(-12.03, 0.8) * mm});
            skLineSegment(sketch, "E54", {"start": v(-12.03, 0.8) * mm, "end": v(-12.03, 0) * mm});
            skLineSegment(sketch, "E55", {"start": v(-12.03, 0) * mm, "end": v(-9.53, 0) * mm});
            skLineSegment(sketch, "E56", {"start": v(0, 28.58) * mm, "end": v(-0.8, 28.58) * mm});
            skLineSegment(sketch, "E57.1.0.0", {"start": v(-31.08, 0.8) * mm, "end": v(-31.08, 0) * mm});
            skLineSegment(sketch, "E57.1.0.1", {"start": v(-26.08, 0) * mm, "end": v(-26.08, 0.8) * mm});
            skLineSegment(sketch, "E57.2.0.0", {"start": v(-50.13, 0.8) * mm, "end": v(-50.13, 0) * mm});
            skLineSegment(sketch, "E57.2.0.1", {"start": v(-45.13, 0) * mm, "end": v(-45.13, 0.8) * mm});
            skLineSegment(sketch, "E57.direction1", {"start": v(-12.03, 0) * mm, "end": v(-31.08, 0) * mm, "construction": true});
            skLineSegment(sketch, "E58.MirrorCS", {"start": v(-12.02, 56.35) * mm, "end": v(-12.02, 57.15) * mm});
            skLineSegment(sketch, "E59.MirrorCS", {"start": v(-7.02, 57.15) * mm, "end": v(-7.02, 56.35) * mm});
            skLineSegment(sketch, "E60.MirrorCS", {"start": v(-26.07, 57.15) * mm, "end": v(-26.07, 56.35) * mm});
            skLineSegment(sketch, "E61.MirrorCS", {"start": v(-31.07, 56.35) * mm, "end": v(-31.07, 57.15) * mm});
            skLineSegment(sketch, "E62.MirrorCS", {"start": v(-45.12, 57.15) * mm, "end": v(-45.12, 56.35) * mm});
            skLineSegment(sketch, "E63.MirrorCS", {"start": v(-50.12, 56.35) * mm, "end": v(-50.12, 57.15) * mm});
            skLineSegment(sketch, "E64", {"start": v(-20.38, 2.63) * mm, "end": v(-17.73, 2.63) * mm});
            skLineSegment(sketch, "E65", {"start": v(-17.73, 2.63) * mm, "end": v(-19.05, 2.63) * mm});
            skLineSegment(sketch, "E66", {"start": v(-19.05, 2.63) * mm, "end": v(-19.05, 0.8) * mm});
            skLineSegment(sketch, "E67", {"start": v(-19.05, 0.8) * mm, "end": v(-16.45, 0.8) * mm});
            skLineSegment(sketch, "E68", {"start": v(-16.45, 0.8) * mm, "end": v(-16.45, 1.6) * mm});
            skLineSegment(sketch, "E69", {"start": v(-16.45, 1.6) * mm, "end": v(-21.65, 1.6) * mm});
            skLineSegment(sketch, "E70", {"start": v(-21.65, 1.6) * mm, "end": v(-21.65, 0.8) * mm});
            skLineSegment(sketch, "E71", {"start": v(-21.65, 0.8) * mm, "end": v(-19.05, 0.8) * mm});
            skLineSegment(sketch, "E72", {"start": v(-39.43, 2.63) * mm, "end": v(-36.78, 2.63) * mm});
            skLineSegment(sketch, "E73", {"start": v(-36.78, 2.63) * mm, "end": v(-38.1, 2.63) * mm});
            skLineSegment(sketch, "E74", {"start": v(-38.1, 2.63) * mm, "end": v(-38.1, 0.8) * mm});
            skLineSegment(sketch, "E75", {"start": v(-38.1, 0.8) * mm, "end": v(-35.5, 0.8) * mm});
            skLineSegment(sketch, "E76", {"start": v(-35.5, 0.8) * mm, "end": v(-35.5, 1.6) * mm});
            skLineSegment(sketch, "E77", {"start": v(-35.5, 1.6) * mm, "end": v(-40.7, 1.6) * mm});
            skLineSegment(sketch, "E78", {"start": v(-40.7, 1.6) * mm, "end": v(-40.7, 0.8) * mm});
            skLineSegment(sketch, "E79", {"start": v(-40.7, 0.8) * mm, "end": v(-38.1, 0.8) * mm});
            skLineSegment(sketch, "E80.MirrorCS", {"start": v(-16.45, 55.55) * mm, "end": v(-21.65, 55.55) * mm});
            skLineSegment(sketch, "E81.MirrorCS", {"start": v(-21.65, 55.55) * mm, "end": v(-21.65, 56.35) * mm});
            skLineSegment(sketch, "E82.MirrorCS", {"start": v(-16.45, 56.35) * mm, "end": v(-16.45, 55.55) * mm});
            skLineSegment(sketch, "E83.MirrorCS", {"start": v(-35.5, 56.35) * mm, "end": v(-35.5, 55.55) * mm});
            skLineSegment(sketch, "E84.MirrorCS", {"start": v(-35.5, 55.55) * mm, "end": v(-40.7, 55.55) * mm});
            skLineSegment(sketch, "E85.MirrorCS", {"start": v(-40.7, 55.55) * mm, "end": v(-40.7, 56.35) * mm});
            skLineSegment(sketch, "E86.bottom", {"start": v(-0.8, 21.43) * mm, "end": v(-1.6, 21.43) * mm});
            skLineSegment(sketch, "E86.top", {"start": v(-0.8, 16.42) * mm, "end": v(-1.6, 16.42) * mm});
            skLineSegment(sketch, "E86.left", {"start": v(-0.8, 21.43) * mm, "end": v(-0.8, 16.42) * mm});
            skLineSegment(sketch, "E86.right", {"start": v(-1.6, 21.43) * mm, "end": v(-1.6, 16.42) * mm});
            skLineSegment(sketch, "E87.bottom", {"start": v(-1.6, 40.72) * mm, "end": v(-0.8, 40.72) * mm});
            skLineSegment(sketch, "E87.top", {"start": v(-1.6, 35.73) * mm, "end": v(-0.8, 35.73) * mm});
            skLineSegment(sketch, "E87.left", {"start": v(-1.6, 40.72) * mm, "end": v(-1.6, 35.73) * mm});
            skLineSegment(sketch, "E87.right", {"start": v(-0.8, 40.72) * mm, "end": v(-0.8, 35.73) * mm});
            skLineSegment(sketch, "E88.MirrorCS", {"start": v(-55.55, 40.72) * mm, "end": v(-55.55, 35.73) * mm});
            skLineSegment(sketch, "E89.MirrorCS", {"start": v(-55.55, 40.72) * mm, "end": v(-56.35, 40.72) * mm});
            skLineSegment(sketch, "E90.MirrorCS", {"start": v(-55.55, 35.73) * mm, "end": v(-56.35, 35.73) * mm});
            skLineSegment(sketch, "E91.MirrorCS", {"start": v(-56.35, 16.42) * mm, "end": v(-55.55, 16.42) * mm});
            skLineSegment(sketch, "E92.MirrorCS", {"start": v(-55.55, 21.43) * mm, "end": v(-55.55, 16.42) * mm});
            skLineSegment(sketch, "E93.MirrorCS", {"start": v(-56.35, 21.43) * mm, "end": v(-55.55, 21.43) * mm});
            skSolve(sketch);
        }
        {
            var Q0;
            {var subQ3=sQuery(id+"F2.wireOp",EDGE,"E58.MirrorCS");Q0=makeQuery(id+"F2.imprint","IMPRINT",FACE,{"disambiguationData":[TD([[makeQuery(id+"F2.imprint","IMPRINT",EDGE,{"derivedFrom":subQ3}),1.0]])]});}
            var Q1;
            {var subQ2=sQuery(id+"F2.wireOp",EDGE,"E61.MirrorCS");Q1=makeQuery(id+"F2.imprint","IMPRINT",FACE,{"disambiguationData":[TD([[makeQuery(id+"F2.imprint","IMPRINT",EDGE,{"derivedFrom":subQ2}),1.0]])]});}
            var Q2;
            {var subQ3=sQuery(id+"F2.wireOp",EDGE,"E54");Q2=makeQuery(id+"F2.imprint","IMPRINT",FACE,{"disambiguationData":[TD([[makeQuery(id+"F2.imprint","IMPRINT",EDGE,{"derivedFrom":subQ3}),-1.0]])]});}
            var Q3;
            {var subQ3=sQuery(id+"F2.wireOp",EDGE,"E57.1.0.0");Q3=makeQuery(id+"F2.imprint","IMPRINT",FACE,{"disambiguationData":[TD([[makeQuery(id+"F2.imprint","IMPRINT",EDGE,{"derivedFrom":subQ3}),-1.0]])]});}
            var Q4;
            {var subQ0=sQuery(id+"F2.wireOp",EDGE,"E43.MirrorCS");Q4=makeQuery(id+"F2.imprint","IMPRINT",FACE,{"disambiguationData":[TD([[makeQuery(id+"F2.imprint","IMPRINT",EDGE,{"derivedFrom":subQ0}),-1.0]])]});}
            var Q5;
            {var subQ3=sQuery(id+"F2.wireOp",EDGE,"E45.MirrorCS");Q5=makeQuery(id+"F2.imprint","IMPRINT",FACE,{"disambiguationData":[TD([[makeQuery(id+"F2.imprint","IMPRINT",EDGE,{"derivedFrom":subQ3}),-1.0]])]});}
            var Q6;
            {var subQ3=sQuery(id+"F2.wireOp",EDGE,"E41.0.1.0");Q6=makeQuery(id+"F2.imprint","IMPRINT",FACE,{"disambiguationData":[TD([[makeQuery(id+"F2.imprint","IMPRINT",EDGE,{"derivedFrom":subQ3}),1.0]])]});}
            var Q7;
            {var subQ0=sQuery(id+"F2.wireOp",EDGE,"E38.MirrorCS");Q7=makeQuery(id+"F2.imprint","IMPRINT",FACE,{"disambiguationData":[TD([[makeQuery(id+"F2.imprint","IMPRINT",EDGE,{"derivedFrom":subQ0}),1.0]])]});}
            var Q8;
            {var subQ0=sQuery(id+"F2.wireOp",EDGE,"E47.MirrorCS");Q8=makeQuery(id+"F2.imprint","IMPRINT",FACE,{"disambiguationData":[TD([[makeQuery(id+"F2.imprint","IMPRINT",EDGE,{"derivedFrom":subQ0}),-1.0]])]});}
            var Q9;
            {var subQ4=sQuery(id+"F2.wireOp",EDGE,"E41.0.2.0");Q9=makeQuery(id+"F2.imprint","IMPRINT",FACE,{"disambiguationData":[TD([[makeQuery(id+"F2.imprint","IMPRINT",EDGE,{"derivedFrom":subQ4}),1.0]])]});}
            var Q10;
            {var subQ3=sQuery(id+"F2.wireOp",EDGE,"E36");Q10=makeQuery(id+"F2.imprint","IMPRINT",FACE,{"disambiguationData":[TD([[makeQuery(id+"F2.imprint","IMPRINT",EDGE,{"derivedFrom":subQ3}),-1.0]])]});}
            var Q11;
            {var subQ3=sQuery(id+"F2.wireOp",EDGE,"E42.MirrorCS");Q11=makeQuery(id+"F2.imprint","IMPRINT",FACE,{"disambiguationData":[TD([[makeQuery(id+"F2.imprint","IMPRINT",EDGE,{"derivedFrom":subQ3}),1.0]])]});}
            var Q12;
            Q12=makeQuery(id+"F2.imprint","IMPRINT",FACE,{"disambiguationData":[TD([[makeQuery(id+"F2.imprint","IMPRINT",EDGE,{"derivedFrom":sQuery(id+"F2.wireOp",EDGE,"seCvFWz7-3Vyj-EDlB-MZ3c-75n9qILX0sIo.bottom")}),1.0]])]});
            var Q13;
            Q13=makeQuery(id+"F2.imprint","IMPRINT",FACE,{"disambiguationData":[TD([[makeQuery(id+"F2.imprint","IMPRINT",EDGE,{"derivedFrom":sQuery(id+"F2.wireOp",EDGE,"4fgsFxhj-Vw8K-A3UU-hoMM-U5Z05xPXw9eo.bottom")}),-1.0]])]});
            var Q14;
            Q14=makeQuery(id+"F2.imprint","IMPRINT",FACE,{"disambiguationData":[TD([[makeQuery(id+"F2.imprint","IMPRINT",EDGE,{"derivedFrom":sQuery(id+"F2.wireOp",EDGE,"8JcU31iA-pnQ1-UeEB-hfCA-LhXNwB3ENcUS.bottom")}),-1.0]])]});
            var Q15;
            Q15=makeQuery(id+"F2.imprint","IMPRINT",FACE,{"disambiguationData":[TD([[makeQuery(id+"F2.imprint","IMPRINT",EDGE,{"derivedFrom":sQuery(id+"F2.wireOp",EDGE,"OlrV4xQ8-PCdh-Lz6a-d3HF-mxwQSlMNRf3y.bottom")}),-1.0]])]});
            var Q16;
            Q16=makeQuery(id+"F2.imprint","IMPRINT",FACE,{"disambiguationData":[TD([[makeQuery(id+"F2.imprint","IMPRINT",EDGE,{"derivedFrom":sQuery(id+"F2.wireOp",EDGE,"ayyhUnhM-DQ2w-0yUz-URMn-H04yOfpyqTR6.bottom")}),-1.0]])]});
            var Q17;
            Q17=makeQuery(id+"F2.imprint","IMPRINT",FACE,{"disambiguationData":[TD([[makeQuery(id+"F2.imprint","IMPRINT",EDGE,{"derivedFrom":sQuery(id+"F2.wireOp",EDGE,"mYwaf8O3-GN9M-ZloA-LC7I-NsK6HDQISpYx.bottom")}),1.0]])]});
            var Q18;
            Q18=makeQuery(id+"F2.imprint","IMPRINT",FACE,{"disambiguationData":[TD([[makeQuery(id+"F2.imprint","IMPRINT",EDGE,{"derivedFrom":sQuery(id+"F2.wireOp",EDGE,"zB8xGJEq-JO7T-5BuP-HgzV-HP2KxO2sEsJY.bottom")}),-1.0]])]});
            var Q19;
            Q19=makeQuery(id+"F2.imprint","IMPRINT",FACE,{"disambiguationData":[TD([[makeQuery(id+"F2.imprint","IMPRINT",EDGE,{"derivedFrom":sQuery(id+"F2.wireOp",EDGE,"NLDKiq9c-kwNa-TPA2-ByV7-jquoLVFJqgiB.bottom")}),1.0]])]});
            var Q20;
            {var subQ0=sQuery(id+"F2.wireOp",EDGE,"E83.MirrorCS");Q20=makeQuery(id+"F2.imprint","IMPRINT",FACE,{"disambiguationData":[TD([[makeQuery(id+"F2.imprint","IMPRINT",EDGE,{"derivedFrom":subQ0}),-1.0]])]});}
            var Q21;
            Q21=makeQuery(id+"F2.imprint","IMPRINT",FACE,{"disambiguationData":[TD([[makeQuery(id+"F2.imprint","IMPRINT",EDGE,{"derivedFrom":sQuery(id+"F2.wireOp",EDGE,"E80.MirrorCS")}),-1.0]])]});
            var Q22;
            {var subQ4=sQuery(id+"F2.wireOp",EDGE,"hzmNtcyy-bsN6-4v00-7gln-cizqo3i05FAj.left");Q22=makeQuery(id+"F2.imprint","IMPRINT",FACE,{"disambiguationData":[TD([[makeQuery(id+"F2.imprint","IMPRINT",EDGE,{"derivedFrom":subQ4}),1.0]])]});}
            var Q23;
            {var subQ0=sQuery(id+"F2.wireOp",EDGE,"9bc7Yqau-rKPS-AFyk-DTsL-w0k6h2iHsBrv");Q23=makeQuery(id+"F2.imprint","IMPRINT",FACE,{"disambiguationData":[TD([[makeQuery(id+"F2.imprint","IMPRINT",EDGE,{"derivedFrom":subQ0}),1.0]])]});}
            var Q24;
            {var subQ0=sQuery(id+"F2.wireOp",EDGE,"uin3CZHS-8rT3-K8BR-KSBn-ANNy8O3vVnNV");Q24=makeQuery(id+"F2.imprint","IMPRINT",FACE,{"disambiguationData":[TD([[makeQuery(id+"F2.imprint","IMPRINT",EDGE,{"derivedFrom":subQ0}),-1.0]])]});}
            var Q25;
            {var subQ1=sQuery(id+"F2.wireOp",EDGE,"9bc7Yqau-rKPS-AFyk-DTsL-w0k6h2iHsBrv");Q25=makeQuery(id+"F2.imprint","IMPRINT",FACE,{"disambiguationData":[TD([[makeQuery(id+"F2.imprint","IMPRINT",EDGE,{"derivedFrom":subQ1}),-1.0]])]});}
            var Q26;
            {var subQ4=sQuery(id+"F2.wireOp",EDGE,"51b707c6-7d05-4d95-a325-fbbc0b48f4530.MirrorCS");Q26=makeQuery(id+"F2.imprint","IMPRINT",FACE,{"disambiguationData":[TD([[makeQuery(id+"F2.imprint","IMPRINT",EDGE,{"derivedFrom":subQ4}),-1.0]])]});}
            var Q27;
            {var subQ3=sQuery(id+"F2.wireOp",EDGE,"E78");Q27=makeQuery(id+"F2.imprint","IMPRINT",FACE,{"disambiguationData":[TD([[makeQuery(id+"F2.imprint","IMPRINT",EDGE,{"derivedFrom":subQ3}),1.0]])]});}
            var Q28;
            {var subQ3=sQuery(id+"F2.wireOp",EDGE,"E76");Q28=makeQuery(id+"F2.imprint","IMPRINT",FACE,{"disambiguationData":[TD([[makeQuery(id+"F2.imprint","IMPRINT",EDGE,{"derivedFrom":subQ3}),1.0]])]});}
            var Q29;
            {var subQ3=sQuery(id+"F2.wireOp",EDGE,"E70");Q29=makeQuery(id+"F2.imprint","IMPRINT",FACE,{"disambiguationData":[TD([[makeQuery(id+"F2.imprint","IMPRINT",EDGE,{"derivedFrom":subQ3}),1.0]])]});}
            var Q30;
            {var subQ3=sQuery(id+"F2.wireOp",EDGE,"E68");Q30=makeQuery(id+"F2.imprint","IMPRINT",FACE,{"disambiguationData":[TD([[makeQuery(id+"F2.imprint","IMPRINT",EDGE,{"derivedFrom":subQ3}),1.0]])]});}
            var Q31;
            {var subQ4=sQuery(id+"F2.wireOp",EDGE,"c7c54e78-877c-4306-874e-dcac1cb5a3220.MirrorCS");Q31=makeQuery(id+"F2.imprint","IMPRINT",FACE,{"disambiguationData":[TD([[makeQuery(id+"F2.imprint","IMPRINT",EDGE,{"derivedFrom":subQ4}),1.0]])]});}
            var Q32;
            {var subQ4=sQuery(id+"F2.wireOp",EDGE,"E88.MirrorCS");Q32=makeQuery(id+"F2.imprint","IMPRINT",FACE,{"disambiguationData":[TD([[makeQuery(id+"F2.imprint","IMPRINT",EDGE,{"derivedFrom":subQ4}),-1.0]])]});}
            var Q33;
            {var subQ4=sQuery(id+"F2.wireOp",EDGE,"E92.MirrorCS");Q33=makeQuery(id+"F2.imprint","IMPRINT",FACE,{"disambiguationData":[TD([[makeQuery(id+"F2.imprint","IMPRINT",EDGE,{"derivedFrom":subQ4}),-1.0]])]});}
            var Q34;
            {var subQ2=sQuery(id+"F2.wireOp",EDGE,"E87.left");Q34=makeQuery(id+"F2.imprint","IMPRINT",FACE,{"disambiguationData":[TD([[makeQuery(id+"F2.imprint","IMPRINT",EDGE,{"derivedFrom":subQ2}),1.0]])]});}
            var Q35;
            {var subQ4=sQuery(id+"F2.wireOp",EDGE,"E86.right");Q35=makeQuery(id+"F2.imprint","IMPRINT",FACE,{"disambiguationData":[TD([[makeQuery(id+"F2.imprint","IMPRINT",EDGE,{"derivedFrom":subQ4}),1.0]])]});}
            extrude(context, id + "F3", {"entities" : qUnion([Q0, Q1, Q2, Q3, Q4, Q5, Q6, Q7, Q8, Q9, Q10, Q11, Q12, Q13, Q14, Q15, Q16, Q17, Q18, Q19, Q20, Q21, Q22, Q23, Q24, Q25, Q26, Q27, Q28, Q29, Q30, Q31, Q32, Q33, Q34, Q35]), "operationType" : NewBodyOperationType.ADD, "depth" : 8.2 * mm, "offsetDistance" : 25 * mm});
        }
        {
            var Q0;
            {var subQ0=sQuery(id+"F2.wireOp",EDGE,"E46.MirrorCS");Q0=makeQuery(id+"F2.imprint","IMPRINT",FACE,{"disambiguationData":[TD([[makeQuery(id+"F2.imprint","IMPRINT",EDGE,{"derivedFrom":subQ0}),-1.0]])]});}
            var Q1;
            {var subQ0=sQuery(id+"F2.wireOp",EDGE,"E44.MirrorCS");Q1=makeQuery(id+"F2.imprint","IMPRINT",FACE,{"disambiguationData":[TD([[makeQuery(id+"F2.imprint","IMPRINT",EDGE,{"derivedFrom":subQ0}),-1.0]])]});}
            var Q2;
            {var subQ0=sQuery(id+"F2.wireOp",EDGE,"E42.MirrorCS");Q2=makeQuery(id+"F2.imprint","IMPRINT",FACE,{"disambiguationData":[TD([[makeQuery(id+"F2.imprint","IMPRINT",EDGE,{"derivedFrom":subQ0}),-1.0]])]});}
            var Q3;
            {var subQ0=sQuery(id+"F2.wireOp",EDGE,"E34");Q3=makeQuery(id+"F2.imprint","IMPRINT",FACE,{"disambiguationData":[TD([[makeQuery(id+"F2.imprint","IMPRINT",EDGE,{"derivedFrom":subQ0}),1.0]])]});}
            var Q4;
            {var subQ0=sQuery(id+"F2.wireOp",EDGE,"E34");Q4=makeQuery(id+"F2.imprint","IMPRINT",FACE,{"disambiguationData":[TD([[makeQuery(id+"F2.imprint","IMPRINT",EDGE,{"derivedFrom":subQ0}),-1.0]])]});}
            var Q5;
            {var subQ0=sQuery(id+"F2.wireOp",EDGE,"E41.0.1.0");Q5=makeQuery(id+"F2.imprint","IMPRINT",FACE,{"disambiguationData":[TD([[makeQuery(id+"F2.imprint","IMPRINT",EDGE,{"derivedFrom":subQ0}),-1.0]])]});}
            var Q6;
            {var subQ0=sQuery(id+"F2.wireOp",EDGE,"E41.0.2.0");Q6=makeQuery(id+"F2.imprint","IMPRINT",FACE,{"disambiguationData":[TD([[makeQuery(id+"F2.imprint","IMPRINT",EDGE,{"derivedFrom":subQ0}),-1.0]])]});}
            var Q7;
            {var subQ0=sQuery(id+"F2.wireOp",EDGE,"E62.MirrorCS");Q7=makeQuery(id+"F2.imprint","IMPRINT",FACE,{"disambiguationData":[TD([[makeQuery(id+"F2.imprint","IMPRINT",EDGE,{"derivedFrom":subQ0}),-1.0]])]});}
            var Q8;
            {var subQ0=sQuery(id+"F2.wireOp",EDGE,"E60.MirrorCS");Q8=makeQuery(id+"F2.imprint","IMPRINT",FACE,{"disambiguationData":[TD([[makeQuery(id+"F2.imprint","IMPRINT",EDGE,{"derivedFrom":subQ0}),-1.0]])]});}
            var Q9;
            {var subQ0=sQuery(id+"F2.wireOp",EDGE,"E58.MirrorCS");Q9=makeQuery(id+"F2.imprint","IMPRINT",FACE,{"disambiguationData":[TD([[makeQuery(id+"F2.imprint","IMPRINT",EDGE,{"derivedFrom":subQ0}),-1.0]])]});}
            var Q10;
            {var subQ0=sQuery(id+"F2.wireOp",EDGE,"E57.2.0.0");Q10=makeQuery(id+"F2.imprint","IMPRINT",FACE,{"disambiguationData":[TD([[makeQuery(id+"F2.imprint","IMPRINT",EDGE,{"derivedFrom":subQ0}),1.0]])]});}
            var Q11;
            {var subQ0=sQuery(id+"F2.wireOp",EDGE,"E40");Q11=makeQuery(id+"F2.imprint","IMPRINT",FACE,{"disambiguationData":[TD([[makeQuery(id+"F2.imprint","IMPRINT",EDGE,{"derivedFrom":subQ0}),1.0]])]});}
            var Q12;
            {var subQ0=sQuery(id+"F2.wireOp",EDGE,"E40");Q12=makeQuery(id+"F2.imprint","IMPRINT",FACE,{"disambiguationData":[TD([[makeQuery(id+"F2.imprint","IMPRINT",EDGE,{"derivedFrom":subQ0}),-1.0]])]});}
            var Q13;
            {var subQ0=sQuery(id+"F2.wireOp",EDGE,"E49");Q13=makeQuery(id+"F2.imprint","IMPRINT",FACE,{"disambiguationData":[TD([[makeQuery(id+"F2.imprint","IMPRINT",EDGE,{"derivedFrom":subQ0}),1.0]])]});}
            var Q14;
            {var subQ0=sQuery(id+"F2.wireOp",EDGE,"E49");Q14=makeQuery(id+"F2.imprint","IMPRINT",FACE,{"disambiguationData":[TD([[makeQuery(id+"F2.imprint","IMPRINT",EDGE,{"derivedFrom":subQ0}),-1.0]])]});}
            var Q15;
            {var subQ0=sQuery(id+"F2.wireOp",EDGE,"E41.0.1.1");Q15=makeQuery(id+"F2.imprint","IMPRINT",FACE,{"disambiguationData":[TD([[makeQuery(id+"F2.imprint","IMPRINT",EDGE,{"derivedFrom":subQ0}),1.0]])]});}
            extrude(context, id + "F4", {"entities" : qUnion([Q0, Q1, Q2, Q3, Q4, Q5, Q6, Q7, Q8, Q9, Q10, Q11, Q12, Q13, Q14, Q15]), "operationType" : NewBodyOperationType.ADD, "depth" : 3.2 * mm, "offsetDistance" : 25 * mm});
        }
        {
            var Q0;
            {var subQ0=sQuery(id+"F2.wireOp",EDGE,"E31.right");var subQ1=makeQuery(id+"F2.imprint","INTERSECT",VERTEX,{"derivedFrom":[subQ0,sQuery(id+"F2.wireOp",EDGE,"E46.MirrorCS")]});var subQ3=makeQuery(id+"F2.imprint","INTERSECT",VERTEX,{"derivedFrom":[subQ0,sQuery(id+"F2.wireOp",EDGE,"E44.MirrorCS")]});var subQ4=makeQuery(id+"F2.imprint","INTERSECT",VERTEX,{"derivedFrom":[subQ0,sQuery(id+"F2.wireOp",EDGE,"E45.MirrorCS")]});var subQ5=makeQuery(id+"F2.imprint","INTERSECT",VERTEX,{"derivedFrom":[subQ0,sQuery(id+"F2.wireOp",EDGE,"E42.MirrorCS")]});var subQ6=makeQuery(id+"F2.imprint","INTERSECT",VERTEX,{"derivedFrom":[subQ0,sQuery(id+"F2.wireOp",EDGE,"E43.MirrorCS")]});Q0=makeQuery(id+"F4.boolean.opBoolean","MERGE",FACE,{"derivedFrom":[makeQuery(id+"F3.boolean.opBoolean","MERGE",FACE,{"derivedFrom":[makeQuery(id+"F1.opExtrude","SWEPT_FACE",FACE,{"disambiguationData":[OSD([sQuery(id+"F0.wireOp",EDGE,"E12.right")])]}),makeQuery(id+"F3.opExtrude","SWEPT_FACE",FACE,{"disambiguationData":[OSD([subQ0]),TDD([makeQuery(id+"F2.imprint","IMPRINT",EDGE,{"disambiguationData":[TD([[makeQuery(id+"F2.imprint","INTERSECT",VERTEX,{"derivedFrom":[sQuery(id+"F2.wireOp",EDGE,"E31.bottom"),subQ0]}),-1.0]])],"derivedFrom":subQ0})])]}),makeQuery(id+"F3.opExtrude","SWEPT_FACE",FACE,{"disambiguationData":[OSD([subQ0]),TDD([makeQuery(id+"F2.imprint","IMPRINT",EDGE,{"disambiguationData":[TD([[subQ6,-1.0]])],"derivedFrom":subQ0})])]}),makeQuery(id+"F3.opExtrude","SWEPT_FACE",FACE,{"disambiguationData":[OSD([subQ0]),TDD([makeQuery(id+"F2.imprint","IMPRINT",EDGE,{"disambiguationData":[TD([[subQ4,-1.0]])],"derivedFrom":subQ0})])]}),makeQuery(id+"F3.opExtrude","SWEPT_FACE",FACE,{"disambiguationData":[OSD([subQ0]),TDD([makeQuery(id+"F2.imprint","IMPRINT",EDGE,{"disambiguationData":[TD([[makeQuery(id+"F2.imprint","INTERSECT",VERTEX,{"derivedFrom":[sQuery(id+"F2.wireOp",EDGE,"E31.top"),subQ0]}),1.0]])],"derivedFrom":subQ0})])]})]}),makeQuery(id+"F4.opExtrude","SWEPT_FACE",FACE,{"disambiguationData":[OSD([subQ0]),TDD([makeQuery(id+"F2.imprint","IMPRINT",EDGE,{"disambiguationData":[TD([[subQ5,-1.0]])],"derivedFrom":subQ0})])]}),makeQuery(id+"F4.opExtrude","SWEPT_FACE",FACE,{"disambiguationData":[OSD([subQ0]),TDD([makeQuery(id+"F2.imprint","IMPRINT",EDGE,{"disambiguationData":[TD([[subQ3,-1.0]])],"derivedFrom":subQ0})])]}),makeQuery(id+"F4.opExtrude","SWEPT_FACE",FACE,{"disambiguationData":[OSD([subQ0]),TDD([makeQuery(id+"F2.imprint","IMPRINT",EDGE,{"disambiguationData":[TD([[subQ1,-1.0]])],"derivedFrom":subQ0})])]})]});}
            var sketch = newSketch(context, id + "F5", { "sketchPlane" : qUnion([Q0])});
            skCircle(sketch, "E94", {"center": v(-19.05, 5) * mm, "radius": 1.25 * mm});
            skLineSegment(sketch, "E95", {"start": v(-26.08, 5) * mm, "end": v(-19.05, 5) * mm});
            skLineSegment(sketch, "E96", {"start": v(-19.05, 5) * mm, "end": v(-12.03, 5) * mm});
            skLineSegment(sketch, "E97", {"start": v(-28.58, 5) * mm, "end": v(-28.57, 0) * mm});
            skCircle(sketch, "E98.MirrorC", {"center": v(-38.1, 5) * mm, "radius": 1.25 * mm});
            skSolve(sketch);
        }
        {
            var Q0;
            Q0=makeQuery(id+"F5.imprint","IMPRINT",FACE,{"disambiguationData":[TD([[makeQuery(id+"F5.imprint","IMPRINT",EDGE,{"derivedFrom":sQuery(id+"F5.wireOp",EDGE,"E98.MirrorC")}),-1.0]])]});
            var Q1;
            {var subQ0=sQuery(id+"F5.wireOp",EDGE,"E95");var subQ1=sQuery(id+"F5.wireOp",EDGE,"E94");var subQ2=makeQuery(id+"F5.imprint","INTERSECT",VERTEX,{"derivedFrom":[subQ1,subQ0]});Q1=makeQuery(id+"F5.imprint","IMPRINT",FACE,{"disambiguationData":[TD([[makeQuery(id+"F5.imprint","IMPRINT",EDGE,{"disambiguationData":[TD([[subQ2,1.0]])],"derivedFrom":subQ1}),1.0]])]});}
            var Q2;
            {var subQ0=sQuery(id+"F5.wireOp",EDGE,"E95");var subQ1=sQuery(id+"F5.wireOp",EDGE,"E94");var subQ2=makeQuery(id+"F5.imprint","INTERSECT",VERTEX,{"derivedFrom":[subQ1,subQ0]});Q2=makeQuery(id+"F5.imprint","IMPRINT",FACE,{"disambiguationData":[TD([[makeQuery(id+"F5.imprint","IMPRINT",EDGE,{"disambiguationData":[TD([[subQ2,-1.0]])],"derivedFrom":subQ1}),1.0]])]});}
            extrude(context, id + "F6", {"entities" : qUnion([Q0, Q1, Q2]), "operationType" : NewBodyOperationType.REMOVE, "endBound" : BoundingType.THROUGH_ALL, "oppositeDirection" : true, "depth" : 25 * mm, "offsetDistance" : 25 * mm});
        }
        {
            var Q0;
            {var subQ0=sQuery(id+"F2.wireOp",EDGE,"E31.bottom");var subQ1=makeQuery(id+"F2.imprint","INTERSECT",VERTEX,{"derivedFrom":[subQ0,sQuery(id+"F2.wireOp",EDGE,"E57.2.0.0")]});var subQ3=makeQuery(id+"F2.imprint","INTERSECT",VERTEX,{"derivedFrom":[subQ0,sQuery(id+"F2.wireOp",EDGE,"E40")]});var subQ4=makeQuery(id+"F2.imprint","INTERSECT",VERTEX,{"derivedFrom":[subQ0,sQuery(id+"F2.wireOp",EDGE,"E57.1.0.0")]});var subQ6=makeQuery(id+"F2.imprint","INTERSECT",VERTEX,{"derivedFrom":[subQ0,sQuery(id+"F2.wireOp",EDGE,"E49")]});var subQ7=makeQuery(id+"F2.imprint","INTERSECT",VERTEX,{"derivedFrom":[subQ0,sQuery(id+"F2.wireOp",EDGE,"E54")]});Q0=makeQuery(id+"F4.boolean.opBoolean","MERGE",FACE,{"derivedFrom":[makeQuery(id+"F3.boolean.opBoolean","MERGE",FACE,{"derivedFrom":[makeQuery(id+"F1.opExtrude","SWEPT_FACE",FACE,{"disambiguationData":[OSD([sQuery(id+"F0.wireOp",EDGE,"E12.bottom")])]}),makeQuery(id+"F3.opExtrude","SWEPT_FACE",FACE,{"disambiguationData":[OSD([subQ0]),TDD([makeQuery(id+"F2.imprint","IMPRINT",EDGE,{"disambiguationData":[TD([[makeQuery(id+"F2.imprint","INTERSECT",VERTEX,{"derivedFrom":[subQ0,sQuery(id+"F2.wireOp",EDGE,"E31.left")]}),-1.0]])],"derivedFrom":subQ0})])]}),makeQuery(id+"F3.opExtrude","SWEPT_FACE",FACE,{"disambiguationData":[OSD([subQ0]),TDD([makeQuery(id+"F2.imprint","IMPRINT",EDGE,{"disambiguationData":[TD([[subQ7,-1.0]])],"derivedFrom":subQ0})])]}),makeQuery(id+"F3.opExtrude","SWEPT_FACE",FACE,{"disambiguationData":[OSD([subQ0]),TDD([makeQuery(id+"F2.imprint","IMPRINT",EDGE,{"disambiguationData":[TD([[subQ4,-1.0]])],"derivedFrom":subQ0})])]}),makeQuery(id+"F3.opExtrude","SWEPT_FACE",FACE,{"disambiguationData":[OSD([subQ0]),TDD([makeQuery(id+"F2.imprint","IMPRINT",EDGE,{"disambiguationData":[TD([[makeQuery(id+"F2.imprint","INTERSECT",VERTEX,{"derivedFrom":[subQ0,sQuery(id+"F2.wireOp",EDGE,"E31.right")]}),1.0]])],"derivedFrom":subQ0})])]})]}),makeQuery(id+"F4.opExtrude","SWEPT_FACE",FACE,{"disambiguationData":[OSD([subQ0]),TDD([makeQuery(id+"F2.imprint","IMPRINT",EDGE,{"disambiguationData":[TD([[subQ6,1.0]])],"derivedFrom":subQ0}),makeQuery(id+"F2.imprint","IMPRINT",EDGE,{"disambiguationData":[TD([[subQ6,-1.0]])],"derivedFrom":subQ0})])]}),makeQuery(id+"F4.opExtrude","SWEPT_FACE",FACE,{"disambiguationData":[OSD([subQ0]),TDD([makeQuery(id+"F2.imprint","IMPRINT",EDGE,{"disambiguationData":[TD([[subQ3,1.0]])],"derivedFrom":subQ0}),makeQuery(id+"F2.imprint","IMPRINT",EDGE,{"disambiguationData":[TD([[subQ3,-1.0]])],"derivedFrom":subQ0})])]}),makeQuery(id+"F4.opExtrude","SWEPT_FACE",FACE,{"disambiguationData":[OSD([subQ0]),TDD([makeQuery(id+"F2.imprint","IMPRINT",EDGE,{"disambiguationData":[TD([[subQ1,1.0]])],"derivedFrom":subQ0})])]})]});}
            var sketch = newSketch(context, id + "F7", { "sketchPlane" : qUnion([Q0])});
            skCircle(sketch, "E99", {"center": v(-19.05, 5) * mm, "radius": 1.25 * mm});
            skLineSegment(sketch, "E100", {"start": v(-19.05, 5) * mm, "end": v(-26.08, 5) * mm});
            skLineSegment(sketch, "E101", {"start": v(-19.05, 5) * mm, "end": v(-12.03, 5) * mm});
            skLineSegment(sketch, "E102", {"start": v(-28.58, 5) * mm, "end": v(-28.58, 0) * mm});
            skCircle(sketch, "E103.MirrorC", {"center": v(-38.1, 5) * mm, "radius": 1.25 * mm});
            skSolve(sketch);
        }
        {
            var Q0;
            {var subQ0=sQuery(id+"F7.wireOp",EDGE,"E100");var subQ1=sQuery(id+"F7.wireOp",EDGE,"E99");var subQ2=makeQuery(id+"F7.imprint","INTERSECT",VERTEX,{"derivedFrom":[subQ1,subQ0]});Q0=makeQuery(id+"F7.imprint","IMPRINT",FACE,{"disambiguationData":[TD([[makeQuery(id+"F7.imprint","IMPRINT",EDGE,{"disambiguationData":[TD([[subQ2,1.0]])],"derivedFrom":subQ1}),1.0]])]});}
            var Q1;
            {var subQ0=sQuery(id+"F7.wireOp",EDGE,"E100");var subQ1=sQuery(id+"F7.wireOp",EDGE,"E99");var subQ2=makeQuery(id+"F7.imprint","INTERSECT",VERTEX,{"derivedFrom":[subQ1,subQ0]});Q1=makeQuery(id+"F7.imprint","IMPRINT",FACE,{"disambiguationData":[TD([[makeQuery(id+"F7.imprint","IMPRINT",EDGE,{"disambiguationData":[TD([[subQ2,-1.0]])],"derivedFrom":subQ1}),1.0]])]});}
            var Q2;
            Q2=makeQuery(id+"F7.imprint","IMPRINT",FACE,{"disambiguationData":[TD([[makeQuery(id+"F7.imprint","IMPRINT",EDGE,{"derivedFrom":sQuery(id+"F7.wireOp",EDGE,"bce639fc-65aa-4438-8615-208144ccd1130.MirrorC")}),-1.0]])]});
            var Q3;
            Q3=makeQuery(id+"F7.imprint","IMPRINT",FACE,{"disambiguationData":[TD([[makeQuery(id+"F7.imprint","IMPRINT",EDGE,{"derivedFrom":sQuery(id+"F7.wireOp",EDGE,"E103.MirrorC")}),-1.0]])]});
            extrude(context, id + "F8", {"entities" : qUnion([Q0, Q1, Q2, Q3]), "operationType" : NewBodyOperationType.REMOVE, "endBound" : BoundingType.THROUGH_ALL, "oppositeDirection" : true, "depth" : 25 * mm, "offsetDistance" : 25 * mm});
        }
    });
